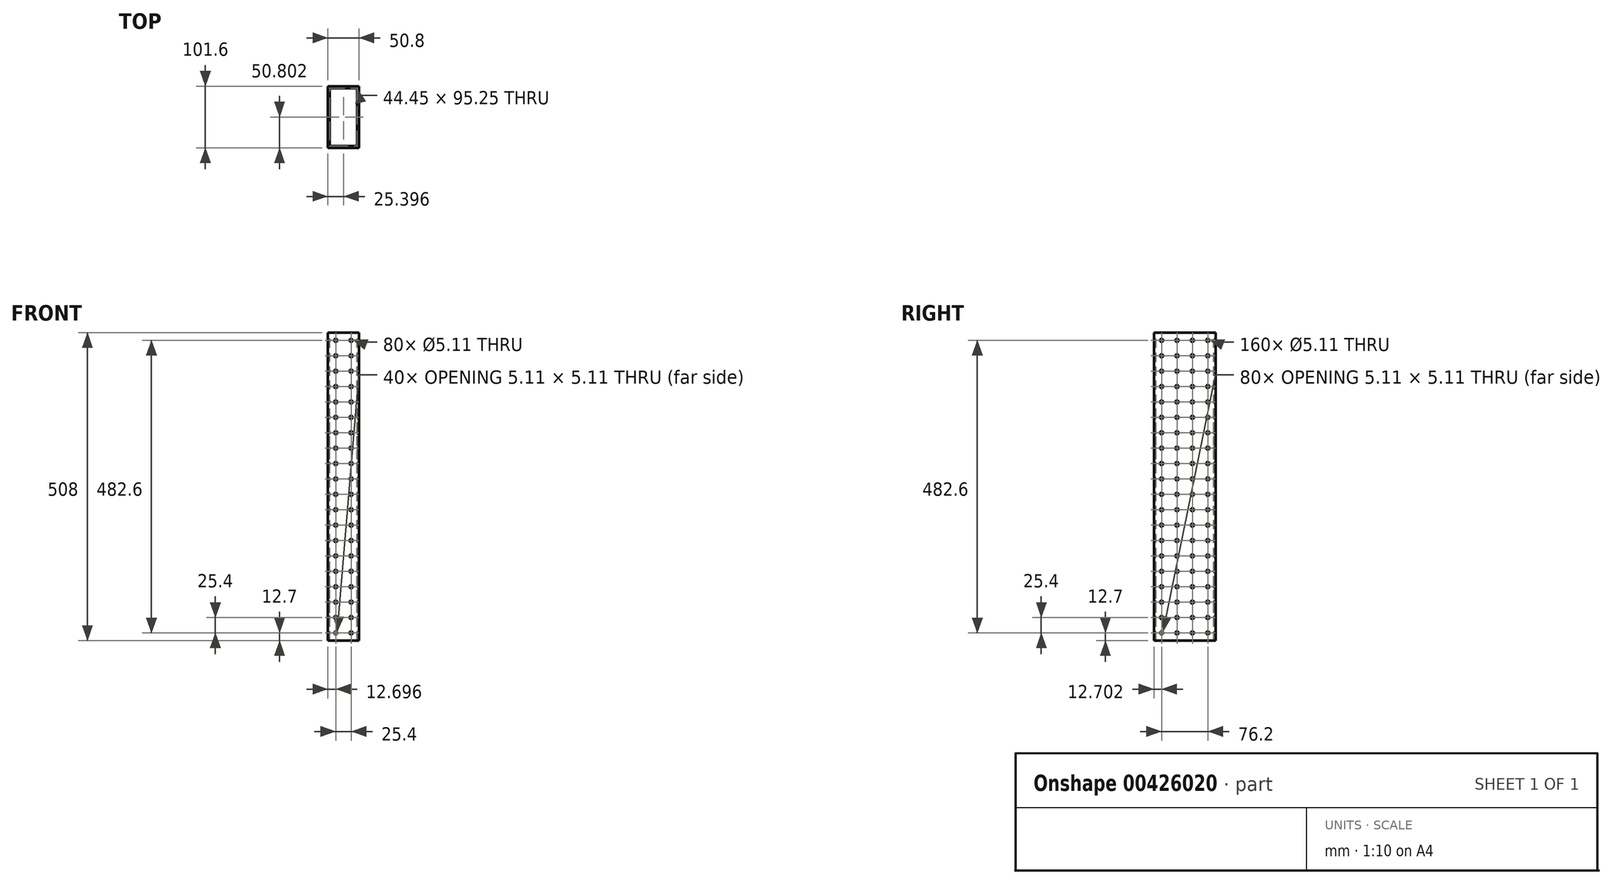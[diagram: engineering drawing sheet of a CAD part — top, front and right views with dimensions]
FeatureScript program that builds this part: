
annotation { "Feature Type Name" : "Feature", "Feature Type Description" : "" }
export const myFeature = defineFeature(function(context is Context, id is Id, definition is map)
    precondition{}
    {
        {
            var Q0;
            Q0=qCreatedBy(makeId("Top.planeOp"),FACE);
            var sketch = newSketch(context, id + "F0", { "sketchPlane" : qUnion([Q0])});
            skLineSegment(sketch, "E0.bottom", {"start": v(-16.8, 74.05) * mm, "end": v(34, 74.05) * mm});
            skLineSegment(sketch, "E0.top", {"start": v(-16.8, -27.55) * mm, "end": v(34, -27.55) * mm});
            skLineSegment(sketch, "E0.left", {"start": v(-16.8, 74.05) * mm, "end": v(-16.8, -27.55) * mm});
            skLineSegment(sketch, "E0.right", {"start": v(34, 74.05) * mm, "end": v(34, -27.55) * mm});
            skSolve(sketch);
        }
        {
            var Q0;
            Q0=makeQuery(id+"F0.imprint","IMPRINT",FACE,{"disambiguationData":[TD([[makeQuery(id+"F0.imprint","IMPRINT",EDGE,{"derivedFrom":sQuery(id+"F0.wireOp",EDGE,"E0.bottom")}),-1.0]])]});
            extrude(context, id + "F1", {"entities" : qUnion([Q0]), "depth" : 508 * mm});
        }
        {
            var Q0;
            Q0=makeQuery(id+"F1.opExtrude","CAP_FACE",FACE,{"disambiguationData":[OSD([sQuery(id+"F0.wireOp",EDGE,"E0.bottom"),sQuery(id+"F0.wireOp",EDGE,"E0.top"),sQuery(id+"F0.wireOp",EDGE,"E0.left"),sQuery(id+"F0.wireOp",EDGE,"E0.right")])],"isStart":false});
            var sketch = newSketch(context, id + "F2", { "sketchPlane" : qUnion([Q0])});
            skLineSegment(sketch, "E1.bottom", {"start": v(-13.63, 70.88) * mm, "end": v(30.82, 70.88) * mm});
            skLineSegment(sketch, "E1.top", {"start": v(-13.63, -24.37) * mm, "end": v(30.82, -24.37) * mm});
            skLineSegment(sketch, "E1.left", {"start": v(-13.63, 70.88) * mm, "end": v(-13.63, -24.37) * mm});
            skLineSegment(sketch, "E1.right", {"start": v(30.82, 70.88) * mm, "end": v(30.82, -24.37) * mm});
            skSolve(sketch);
        }
        {
            var Q0;
            Q0=makeQuery(id+"F2.imprint","IMPRINT",FACE,{"disambiguationData":[TD([[makeQuery(id+"F2.imprint","IMPRINT",EDGE,{"derivedFrom":sQuery(id+"F2.wireOp",EDGE,"E1.bottom")}),-1.0]])]});
            extrude(context, id + "F3", {"entities" : qUnion([Q0]), "operationType" : NewBodyOperationType.REMOVE, "oppositeDirection" : true, "depth" : 508 * mm});
        }
        {
            var Q0;
            Q0=makeQuery(id+"F1.opExtrude","SWEPT_FACE",FACE,{"disambiguationData":[OSD([sQuery(id+"F0.wireOp",EDGE,"E0.right")])]});
            var sketch = newSketch(context, id + "F4", { "sketchPlane" : qUnion([Q0])});
            skCircle(sketch, "E2", {"center": v(61.35, 495.3) * mm, "radius": 2.55 * mm});
            skCircle(sketch, "E3.0.1.0", {"center": v(61.35, 469.9) * mm, "radius": 2.55 * mm});
            skCircle(sketch, "E3.0.2.0", {"center": v(61.35, 444.5) * mm, "radius": 2.55 * mm});
            skCircle(sketch, "E3.0.3.0", {"center": v(61.35, 419.1) * mm, "radius": 2.55 * mm});
            skCircle(sketch, "E3.0.4.0", {"center": v(61.35, 393.7) * mm, "radius": 2.55 * mm});
            skCircle(sketch, "E3.0.5.0", {"center": v(61.35, 368.3) * mm, "radius": 2.55 * mm});
            skCircle(sketch, "E3.0.6.0", {"center": v(61.35, 342.9) * mm, "radius": 2.55 * mm});
            skCircle(sketch, "E3.0.7.0", {"center": v(61.35, 317.5) * mm, "radius": 2.55 * mm});
            skCircle(sketch, "E3.0.8.0", {"center": v(61.35, 292.1) * mm, "radius": 2.55 * mm});
            skCircle(sketch, "E3.0.9.0", {"center": v(61.35, 266.7) * mm, "radius": 2.55 * mm});
            skCircle(sketch, "E3.0.10.0", {"center": v(61.35, 241.3) * mm, "radius": 2.55 * mm});
            skCircle(sketch, "E3.0.11.0", {"center": v(61.35, 215.9) * mm, "radius": 2.55 * mm});
            skCircle(sketch, "E3.0.12.0", {"center": v(61.35, 190.5) * mm, "radius": 2.55 * mm});
            skCircle(sketch, "E3.0.13.0", {"center": v(61.35, 165.1) * mm, "radius": 2.55 * mm});
            skCircle(sketch, "E3.0.14.0", {"center": v(61.35, 139.7) * mm, "radius": 2.55 * mm});
            skCircle(sketch, "E3.0.15.0", {"center": v(61.35, 114.3) * mm, "radius": 2.55 * mm});
            skCircle(sketch, "E3.0.16.0", {"center": v(61.35, 88.9) * mm, "radius": 2.55 * mm});
            skCircle(sketch, "E3.0.17.0", {"center": v(61.35, 63.5) * mm, "radius": 2.55 * mm});
            skCircle(sketch, "E3.0.18.0", {"center": v(61.35, 38.1) * mm, "radius": 2.55 * mm});
            skCircle(sketch, "E3.0.19.0", {"center": v(61.35, 12.7) * mm, "radius": 2.55 * mm});
            skCircle(sketch, "E3.1.0.0", {"center": v(35.95, 495.3) * mm, "radius": 2.55 * mm});
            skCircle(sketch, "E3.1.1.0", {"center": v(35.95, 469.9) * mm, "radius": 2.55 * mm});
            skCircle(sketch, "E3.1.2.0", {"center": v(35.95, 444.5) * mm, "radius": 2.55 * mm});
            skCircle(sketch, "E3.1.3.0", {"center": v(35.95, 419.1) * mm, "radius": 2.55 * mm});
            skCircle(sketch, "E3.1.4.0", {"center": v(35.95, 393.7) * mm, "radius": 2.55 * mm});
            skCircle(sketch, "E3.1.5.0", {"center": v(35.95, 368.3) * mm, "radius": 2.55 * mm});
            skCircle(sketch, "E3.1.6.0", {"center": v(35.95, 342.9) * mm, "radius": 2.55 * mm});
            skCircle(sketch, "E3.1.7.0", {"center": v(35.95, 317.5) * mm, "radius": 2.55 * mm});
            skCircle(sketch, "E3.1.8.0", {"center": v(35.95, 292.1) * mm, "radius": 2.55 * mm});
            skCircle(sketch, "E3.1.9.0", {"center": v(35.95, 266.7) * mm, "radius": 2.55 * mm});
            skCircle(sketch, "E3.1.10.0", {"center": v(35.95, 241.3) * mm, "radius": 2.55 * mm});
            skCircle(sketch, "E3.1.11.0", {"center": v(35.95, 215.9) * mm, "radius": 2.55 * mm});
            skCircle(sketch, "E3.1.12.0", {"center": v(35.95, 190.5) * mm, "radius": 2.55 * mm});
            skCircle(sketch, "E3.1.13.0", {"center": v(35.95, 165.1) * mm, "radius": 2.55 * mm});
            skCircle(sketch, "E3.1.14.0", {"center": v(35.95, 139.7) * mm, "radius": 2.55 * mm});
            skCircle(sketch, "E3.1.15.0", {"center": v(35.95, 114.3) * mm, "radius": 2.55 * mm});
            skCircle(sketch, "E3.1.16.0", {"center": v(35.95, 88.9) * mm, "radius": 2.55 * mm});
            skCircle(sketch, "E3.1.17.0", {"center": v(35.95, 63.5) * mm, "radius": 2.55 * mm});
            skCircle(sketch, "E3.1.18.0", {"center": v(35.95, 38.1) * mm, "radius": 2.55 * mm});
            skCircle(sketch, "E3.1.19.0", {"center": v(35.95, 12.7) * mm, "radius": 2.55 * mm});
            skCircle(sketch, "E3.2.0.0", {"center": v(10.55, 495.3) * mm, "radius": 2.55 * mm});
            skCircle(sketch, "E3.2.1.0", {"center": v(10.55, 469.9) * mm, "radius": 2.55 * mm});
            skCircle(sketch, "E3.2.2.0", {"center": v(10.55, 444.5) * mm, "radius": 2.55 * mm});
            skCircle(sketch, "E3.2.3.0", {"center": v(10.55, 419.1) * mm, "radius": 2.55 * mm});
            skCircle(sketch, "E3.2.4.0", {"center": v(10.55, 393.7) * mm, "radius": 2.55 * mm});
            skCircle(sketch, "E3.2.5.0", {"center": v(10.55, 368.3) * mm, "radius": 2.55 * mm});
            skCircle(sketch, "E3.2.6.0", {"center": v(10.55, 342.9) * mm, "radius": 2.55 * mm});
            skCircle(sketch, "E3.2.7.0", {"center": v(10.55, 317.5) * mm, "radius": 2.55 * mm});
            skCircle(sketch, "E3.2.8.0", {"center": v(10.55, 292.1) * mm, "radius": 2.55 * mm});
            skCircle(sketch, "E3.2.9.0", {"center": v(10.55, 266.7) * mm, "radius": 2.55 * mm});
            skCircle(sketch, "E3.2.10.0", {"center": v(10.55, 241.3) * mm, "radius": 2.55 * mm});
            skCircle(sketch, "E3.2.11.0", {"center": v(10.55, 215.9) * mm, "radius": 2.55 * mm});
            skCircle(sketch, "E3.2.12.0", {"center": v(10.55, 190.5) * mm, "radius": 2.55 * mm});
            skCircle(sketch, "E3.2.13.0", {"center": v(10.55, 165.1) * mm, "radius": 2.55 * mm});
            skCircle(sketch, "E3.2.14.0", {"center": v(10.55, 139.7) * mm, "radius": 2.55 * mm});
            skCircle(sketch, "E3.2.15.0", {"center": v(10.55, 114.3) * mm, "radius": 2.55 * mm});
            skCircle(sketch, "E3.2.16.0", {"center": v(10.55, 88.9) * mm, "radius": 2.55 * mm});
            skCircle(sketch, "E3.2.17.0", {"center": v(10.55, 63.5) * mm, "radius": 2.55 * mm});
            skCircle(sketch, "E3.2.18.0", {"center": v(10.55, 38.1) * mm, "radius": 2.55 * mm});
            skCircle(sketch, "E3.2.19.0", {"center": v(10.55, 12.7) * mm, "radius": 2.55 * mm});
            skCircle(sketch, "E3.3.0.0", {"center": v(-14.85, 495.3) * mm, "radius": 2.55 * mm});
            skCircle(sketch, "E3.3.1.0", {"center": v(-14.85, 469.9) * mm, "radius": 2.55 * mm});
            skCircle(sketch, "E3.3.2.0", {"center": v(-14.85, 444.5) * mm, "radius": 2.55 * mm});
            skCircle(sketch, "E3.3.3.0", {"center": v(-14.85, 419.1) * mm, "radius": 2.55 * mm});
            skCircle(sketch, "E3.3.4.0", {"center": v(-14.85, 393.7) * mm, "radius": 2.55 * mm});
            skCircle(sketch, "E3.3.5.0", {"center": v(-14.85, 368.3) * mm, "radius": 2.55 * mm});
            skCircle(sketch, "E3.3.6.0", {"center": v(-14.85, 342.9) * mm, "radius": 2.55 * mm});
            skCircle(sketch, "E3.3.7.0", {"center": v(-14.85, 317.5) * mm, "radius": 2.55 * mm});
            skCircle(sketch, "E3.3.8.0", {"center": v(-14.85, 292.1) * mm, "radius": 2.55 * mm});
            skCircle(sketch, "E3.3.9.0", {"center": v(-14.85, 266.7) * mm, "radius": 2.55 * mm});
            skCircle(sketch, "E3.3.10.0", {"center": v(-14.85, 241.3) * mm, "radius": 2.55 * mm});
            skCircle(sketch, "E3.3.11.0", {"center": v(-14.85, 215.9) * mm, "radius": 2.55 * mm});
            skCircle(sketch, "E3.3.12.0", {"center": v(-14.85, 190.5) * mm, "radius": 2.55 * mm});
            skCircle(sketch, "E3.3.13.0", {"center": v(-14.85, 165.1) * mm, "radius": 2.55 * mm});
            skCircle(sketch, "E3.3.14.0", {"center": v(-14.85, 139.7) * mm, "radius": 2.55 * mm});
            skCircle(sketch, "E3.3.15.0", {"center": v(-14.85, 114.3) * mm, "radius": 2.55 * mm});
            skCircle(sketch, "E3.3.16.0", {"center": v(-14.85, 88.9) * mm, "radius": 2.55 * mm});
            skCircle(sketch, "E3.3.17.0", {"center": v(-14.85, 63.5) * mm, "radius": 2.55 * mm});
            skCircle(sketch, "E3.3.18.0", {"center": v(-14.85, 38.1) * mm, "radius": 2.55 * mm});
            skCircle(sketch, "E3.3.19.0", {"center": v(-14.85, 12.7) * mm, "radius": 2.55 * mm});
            skLineSegment(sketch, "E3.direction1", {"start": v(61.35, 495.3) * mm, "end": v(35.95, 495.3) * mm, "construction": true});
            skLineSegment(sketch, "E3.direction2", {"start": v(61.35, 495.3) * mm, "end": v(61.35, 469.9) * mm, "construction": true});
            skSolve(sketch);
        }
        {
            var Q0;
            Q0=sQuery(id+"F4.wireOp",VERTEX,"E3.1.15.0.center");
            var Q1;
            Q1=sQuery(id+"F4.wireOp",VERTEX,"E3.0.19.0.center");
            var Q2;
            Q2=sQuery(id+"F4.wireOp",VERTEX,"E3.3.7.0.center");
            var Q3;
            Q3=sQuery(id+"F4.wireOp",VERTEX,"E3.2.11.0.center");
            var Q4;
            Q4=sQuery(id+"F4.wireOp",VERTEX,"E3.3.0.0.center");
            var Q5;
            Q5=sQuery(id+"F4.wireOp",VERTEX,"E3.2.4.0.center");
            var Q6;
            Q6=sQuery(id+"F4.wireOp",VERTEX,"E3.1.8.0.center");
            var Q7;
            Q7=sQuery(id+"F4.wireOp",VERTEX,"E3.0.12.0.center");
            var Q8;
            Q8=sQuery(id+"F4.wireOp",VERTEX,"E3.3.16.0.center");
            var Q9;
            Q9=sQuery(id+"F4.wireOp",VERTEX,"E3.3.8.0.center");
            var Q10;
            Q10=sQuery(id+"F4.wireOp",VERTEX,"E3.2.12.0.center");
            var Q11;
            Q11=sQuery(id+"F4.wireOp",VERTEX,"E3.3.1.0.center");
            var Q12;
            Q12=sQuery(id+"F4.wireOp",VERTEX,"E3.2.5.0.center");
            var Q13;
            Q13=sQuery(id+"F4.wireOp",VERTEX,"E3.1.9.0.center");
            var Q14;
            Q14=sQuery(id+"F4.wireOp",VERTEX,"E3.0.13.0.center");
            var Q15;
            Q15=sQuery(id+"F4.wireOp",VERTEX,"E3.3.17.0.center");
            var Q16;
            Q16=sQuery(id+"F4.wireOp",VERTEX,"E3.1.16.0.center");
            var Q17;
            Q17=sQuery(id+"F4.wireOp",VERTEX,"E3.3.2.0.center");
            var Q18;
            Q18=sQuery(id+"F4.wireOp",VERTEX,"E3.2.6.0.center");
            var Q19;
            Q19=sQuery(id+"F4.wireOp",VERTEX,"E3.1.10.0.center");
            var Q20;
            Q20=sQuery(id+"F4.wireOp",VERTEX,"E3.0.14.0.center");
            var Q21;
            Q21=sQuery(id+"F4.wireOp",VERTEX,"E3.3.18.0.center");
            var Q22;
            Q22=sQuery(id+"F4.wireOp",VERTEX,"E3.1.17.0.center");
            var Q23;
            Q23=sQuery(id+"F4.wireOp",VERTEX,"E3.1.1.0.center");
            var Q24;
            Q24=sQuery(id+"F4.wireOp",VERTEX,"E3.3.9.0.center");
            var Q25;
            Q25=sQuery(id+"F4.wireOp",VERTEX,"E3.2.13.0.center");
            var Q26;
            Q26=sQuery(id+"F4.wireOp",VERTEX,"E3.3.3.0.center");
            var Q27;
            Q27=sQuery(id+"F4.wireOp",VERTEX,"E3.2.7.0.center");
            var Q28;
            Q28=sQuery(id+"F4.wireOp",VERTEX,"E3.1.11.0.center");
            var Q29;
            Q29=sQuery(id+"F4.wireOp",VERTEX,"E3.0.15.0.center");
            var Q30;
            Q30=sQuery(id+"F4.wireOp",VERTEX,"E3.3.19.0.center");
            var Q31;
            Q31=sQuery(id+"F4.wireOp",VERTEX,"E3.1.18.0.center");
            var Q32;
            Q32=sQuery(id+"F4.wireOp",VERTEX,"E3.1.2.0.center");
            var Q33;
            Q33=sQuery(id+"F4.wireOp",VERTEX,"E3.3.10.0.center");
            var Q34;
            Q34=sQuery(id+"F4.wireOp",VERTEX,"E3.2.14.0.center");
            var Q35;
            Q35=sQuery(id+"F4.wireOp",VERTEX,"E3.2.17.0.center");
            var Q36;
            Q36=sQuery(id+"F4.wireOp",VERTEX,"E3.3.4.0.center");
            var Q37;
            Q37=sQuery(id+"F4.wireOp",VERTEX,"E3.2.8.0.center");
            var Q38;
            Q38=sQuery(id+"F4.wireOp",VERTEX,"E3.2.1.0.center");
            var Q39;
            Q39=sQuery(id+"F4.wireOp",VERTEX,"E3.1.5.0.center");
            var Q40;
            Q40=sQuery(id+"F4.wireOp",VERTEX,"E3.1.12.0.center");
            var Q41;
            Q41=sQuery(id+"F4.wireOp",VERTEX,"E3.0.16.0.center");
            var Q42;
            Q42=sQuery(id+"F4.wireOp",VERTEX,"E3.3.13.0.center");
            var Q43;
            Q43=sQuery(id+"F4.wireOp",VERTEX,"E3.1.19.0.center");
            var Q44;
            Q44=sQuery(id+"F4.wireOp",VERTEX,"E3.1.3.0.center");
            var Q45;
            Q45=sQuery(id+"F4.wireOp",VERTEX,"E3.3.11.0.center");
            var Q46;
            Q46=sQuery(id+"F4.wireOp",VERTEX,"E3.2.15.0.center");
            var Q47;
            Q47=sQuery(id+"F4.wireOp",VERTEX,"E3.2.18.0.center");
            var Q48;
            Q48=sQuery(id+"F4.wireOp",VERTEX,"E3.3.5.0.center");
            var Q49;
            Q49=sQuery(id+"F4.wireOp",VERTEX,"E3.2.2.0.center");
            var Q50;
            Q50=sQuery(id+"F4.wireOp",VERTEX,"E3.2.9.0.center");
            var Q51;
            Q51=sQuery(id+"F4.wireOp",VERTEX,"E3.1.6.0.center");
            var Q52;
            Q52=sQuery(id+"F4.wireOp",VERTEX,"E3.1.13.0.center");
            var Q53;
            Q53=sQuery(id+"F4.wireOp",VERTEX,"E3.0.17.0.center");
            var Q54;
            Q54=sQuery(id+"F4.wireOp",VERTEX,"E3.3.14.0.center");
            var Q55;
            Q55=sQuery(id+"F4.wireOp",VERTEX,"E3.2.0.0.center");
            var Q56;
            Q56=sQuery(id+"F4.wireOp",VERTEX,"E3.1.4.0.center");
            var Q57;
            Q57=sQuery(id+"F4.wireOp",VERTEX,"E3.0.9.0.center");
            var Q58;
            Q58=sQuery(id+"F4.wireOp",VERTEX,"E3.0.10.0.center");
            var Q59;
            Q59=sQuery(id+"F4.wireOp",VERTEX,"E3.3.12.0.center");
            var Q60;
            Q60=sQuery(id+"F4.wireOp",VERTEX,"E3.2.16.0.center");
            var Q61;
            Q61=sQuery(id+"F4.wireOp",VERTEX,"E3.0.11.0.center");
            var Q62;
            Q62=sQuery(id+"F4.wireOp",VERTEX,"E3.direction1.end");
            var Q63;
            Q63=sQuery(id+"F4.wireOp",VERTEX,"E2.center");
            var Q64;
            Q64=sQuery(id+"F4.wireOp",VERTEX,"E3.3.6.0.center");
            var Q65;
            Q65=sQuery(id+"F4.wireOp",VERTEX,"E3.2.19.0.center");
            var Q66;
            Q66=sQuery(id+"F4.wireOp",VERTEX,"E3.2.10.0.center");
            var Q67;
            Q67=sQuery(id+"F4.wireOp",VERTEX,"E3.2.3.0.center");
            var Q68;
            Q68=sQuery(id+"F4.wireOp",VERTEX,"E3.1.7.0.center");
            var Q69;
            Q69=sQuery(id+"F4.wireOp",VERTEX,"E3.1.14.0.center");
            var Q70;
            Q70=sQuery(id+"F4.wireOp",VERTEX,"E3.0.18.0.center");
            var Q71;
            Q71=sQuery(id+"F4.wireOp",VERTEX,"E3.0.1.0.center");
            var Q72;
            Q72=sQuery(id+"F4.wireOp",VERTEX,"E3.3.15.0.center");
            var Q73;
            Q73=sQuery(id+"F4.wireOp",VERTEX,"E3.0.2.0.center");
            var Q74;
            Q74=sQuery(id+"F4.wireOp",VERTEX,"E3.0.3.0.center");
            var Q75;
            Q75=sQuery(id+"F4.wireOp",VERTEX,"E3.0.4.0.center");
            var Q76;
            Q76=sQuery(id+"F4.wireOp",VERTEX,"E3.0.5.0.center");
            var Q77;
            Q77=sQuery(id+"F4.wireOp",VERTEX,"E3.0.6.0.center");
            var Q78;
            Q78=sQuery(id+"F4.wireOp",VERTEX,"E3.0.7.0.center");
            var Q79;
            Q79=sQuery(id+"F4.wireOp",VERTEX,"E3.0.8.0.center");
            var Q80;
            Q80=makeQuery(id+"F1.opExtrude","SWEPT_BODY",BODY,{"disambiguationData":[OSD([sQuery(id+"F0.wireOp",EDGE,"E0.bottom"),sQuery(id+"F0.wireOp",EDGE,"E0.top"),sQuery(id+"F0.wireOp",EDGE,"E0.left"),sQuery(id+"F0.wireOp",EDGE,"E0.right")])]});
            hole(context, id + "F5", {"style" : HoleStyle.SIMPLE, "endStyle" : HoleEndStyle.THROUGH, "holeDiameter" : 5.1 * mm, "isTappedThrough" : true, "tappedDepth" : 12.7 * mm, "tapClearance" : 3, "locations" : qUnion([Q0, Q1, Q2, Q3, Q4, Q5, Q6, Q7, Q8, Q9, Q10, Q11, Q12, Q13, Q14, Q15, Q16, Q17, Q18, Q19, Q20, Q21, Q22, Q23, Q24, Q25, Q26, Q27, Q28, Q29, Q30, Q31, Q32, Q33, Q34, Q35, Q36, Q37, Q38, Q39, Q40, Q41, Q42, Q43, Q44, Q45, Q46, Q47, Q48, Q49, Q50, Q51, Q52, Q53, Q54, Q55, Q56, Q57, Q58, Q59, Q60, Q61, Q62, Q63, Q64, Q65, Q66, Q67, Q68, Q69, Q70, Q71, Q72, Q73, Q74, Q75, Q76, Q77, Q78, Q79]), "scope" : qUnion([Q80])});
        }
        {
            var Q0;
            Q0=makeQuery(id+"F1.opExtrude","SWEPT_FACE",FACE,{"disambiguationData":[OSD([sQuery(id+"F0.wireOp",EDGE,"E0.bottom")])]});
            var sketch = newSketch(context, id + "F6", { "sketchPlane" : qUnion([Q0])});
            skCircle(sketch, "E4", {"center": v(-21.3, 495.3) * mm, "radius": 2.55 * mm});
            skCircle(sketch, "E5.0.1.0", {"center": v(-21.3, 469.9) * mm, "radius": 2.55 * mm});
            skCircle(sketch, "E5.0.2.0", {"center": v(-21.3, 444.5) * mm, "radius": 2.55 * mm});
            skCircle(sketch, "E5.0.3.0", {"center": v(-21.3, 419.1) * mm, "radius": 2.55 * mm});
            skCircle(sketch, "E5.0.4.0", {"center": v(-21.3, 393.7) * mm, "radius": 2.55 * mm});
            skCircle(sketch, "E5.0.5.0", {"center": v(-21.3, 368.3) * mm, "radius": 2.55 * mm});
            skCircle(sketch, "E5.0.6.0", {"center": v(-21.3, 342.9) * mm, "radius": 2.55 * mm});
            skCircle(sketch, "E5.0.7.0", {"center": v(-21.3, 317.5) * mm, "radius": 2.55 * mm});
            skCircle(sketch, "E5.0.8.0", {"center": v(-21.3, 292.1) * mm, "radius": 2.55 * mm});
            skCircle(sketch, "E5.0.9.0", {"center": v(-21.3, 266.7) * mm, "radius": 2.55 * mm});
            skCircle(sketch, "E5.0.10.0", {"center": v(-21.3, 241.3) * mm, "radius": 2.55 * mm});
            skCircle(sketch, "E5.0.11.0", {"center": v(-21.3, 215.9) * mm, "radius": 2.55 * mm});
            skCircle(sketch, "E5.0.12.0", {"center": v(-21.3, 190.5) * mm, "radius": 2.55 * mm});
            skCircle(sketch, "E5.0.13.0", {"center": v(-21.3, 165.1) * mm, "radius": 2.55 * mm});
            skCircle(sketch, "E5.0.14.0", {"center": v(-21.3, 139.7) * mm, "radius": 2.55 * mm});
            skCircle(sketch, "E5.0.15.0", {"center": v(-21.3, 114.3) * mm, "radius": 2.55 * mm});
            skCircle(sketch, "E5.0.16.0", {"center": v(-21.3, 88.9) * mm, "radius": 2.55 * mm});
            skCircle(sketch, "E5.0.17.0", {"center": v(-21.3, 63.5) * mm, "radius": 2.55 * mm});
            skCircle(sketch, "E5.0.18.0", {"center": v(-21.3, 38.1) * mm, "radius": 2.55 * mm});
            skCircle(sketch, "E5.0.19.0", {"center": v(-21.3, 12.7) * mm, "radius": 2.55 * mm});
            skCircle(sketch, "E5.1.0.0", {"center": v(4.1, 495.3) * mm, "radius": 2.55 * mm});
            skCircle(sketch, "E5.1.1.0", {"center": v(4.1, 469.9) * mm, "radius": 2.55 * mm});
            skCircle(sketch, "E5.1.2.0", {"center": v(4.1, 444.5) * mm, "radius": 2.55 * mm});
            skCircle(sketch, "E5.1.3.0", {"center": v(4.1, 419.1) * mm, "radius": 2.55 * mm});
            skCircle(sketch, "E5.1.4.0", {"center": v(4.1, 393.7) * mm, "radius": 2.55 * mm});
            skCircle(sketch, "E5.1.5.0", {"center": v(4.1, 368.3) * mm, "radius": 2.55 * mm});
            skCircle(sketch, "E5.1.6.0", {"center": v(4.1, 342.9) * mm, "radius": 2.55 * mm});
            skCircle(sketch, "E5.1.7.0", {"center": v(4.1, 317.5) * mm, "radius": 2.55 * mm});
            skCircle(sketch, "E5.1.8.0", {"center": v(4.1, 292.1) * mm, "radius": 2.55 * mm});
            skCircle(sketch, "E5.1.9.0", {"center": v(4.1, 266.7) * mm, "radius": 2.55 * mm});
            skCircle(sketch, "E5.1.10.0", {"center": v(4.1, 241.3) * mm, "radius": 2.55 * mm});
            skCircle(sketch, "E5.1.11.0", {"center": v(4.1, 215.9) * mm, "radius": 2.55 * mm});
            skCircle(sketch, "E5.1.12.0", {"center": v(4.1, 190.5) * mm, "radius": 2.55 * mm});
            skCircle(sketch, "E5.1.13.0", {"center": v(4.1, 165.1) * mm, "radius": 2.55 * mm});
            skCircle(sketch, "E5.1.14.0", {"center": v(4.1, 139.7) * mm, "radius": 2.55 * mm});
            skCircle(sketch, "E5.1.15.0", {"center": v(4.1, 114.3) * mm, "radius": 2.55 * mm});
            skCircle(sketch, "E5.1.16.0", {"center": v(4.1, 88.9) * mm, "radius": 2.55 * mm});
            skCircle(sketch, "E5.1.17.0", {"center": v(4.1, 63.5) * mm, "radius": 2.55 * mm});
            skCircle(sketch, "E5.1.18.0", {"center": v(4.1, 38.1) * mm, "radius": 2.55 * mm});
            skCircle(sketch, "E5.1.19.0", {"center": v(4.1, 12.7) * mm, "radius": 2.55 * mm});
            skLineSegment(sketch, "E5.direction1", {"start": v(-21.3, 495.3) * mm, "end": v(4.1, 495.3) * mm, "construction": true});
            skLineSegment(sketch, "E5.direction2", {"start": v(-21.3, 495.3) * mm, "end": v(-21.3, 469.9) * mm, "construction": true});
            skSolve(sketch);
        }
        {
            var Q0;
            Q0=sQuery(id+"F6.wireOp",VERTEX,"E5.0.11.0.center");
            var Q1;
            Q1=sQuery(id+"F6.wireOp",VERTEX,"E5.0.10.0.center");
            var Q2;
            Q2=sQuery(id+"F6.wireOp",VERTEX,"E5.0.15.0.center");
            var Q3;
            Q3=sQuery(id+"F6.wireOp",VERTEX,"E5.1.11.0.center");
            var Q4;
            Q4=sQuery(id+"F6.wireOp",VERTEX,"E5.1.2.0.center");
            var Q5;
            Q5=sQuery(id+"F6.wireOp",VERTEX,"E5.1.18.0.center");
            var Q6;
            Q6=sQuery(id+"F6.wireOp",VERTEX,"E5.0.9.0.center");
            var Q7;
            Q7=sQuery(id+"F6.wireOp",VERTEX,"E5.0.8.0.center");
            var Q8;
            Q8=sQuery(id+"F6.wireOp",VERTEX,"E5.0.7.0.center");
            var Q9;
            Q9=sQuery(id+"F6.wireOp",VERTEX,"E5.0.2.0.center");
            var Q10;
            Q10=sQuery(id+"F6.wireOp",VERTEX,"E5.0.1.0.center");
            var Q11;
            Q11=sQuery(id+"F6.wireOp",VERTEX,"E5.0.4.0.center");
            var Q12;
            Q12=sQuery(id+"F6.wireOp",VERTEX,"E5.0.3.0.center");
            var Q13;
            Q13=sQuery(id+"F6.wireOp",VERTEX,"E5.0.6.0.center");
            var Q14;
            Q14=sQuery(id+"F6.wireOp",VERTEX,"E5.0.5.0.center");
            var Q15;
            Q15=sQuery(id+"F6.wireOp",VERTEX,"E5.0.14.0.center");
            var Q16;
            Q16=sQuery(id+"F6.wireOp",VERTEX,"E5.1.10.0.center");
            var Q17;
            Q17=sQuery(id+"F6.wireOp",VERTEX,"E5.1.1.0.center");
            var Q18;
            Q18=sQuery(id+"F6.wireOp",VERTEX,"E5.1.17.0.center");
            var Q19;
            Q19=sQuery(id+"F6.wireOp",VERTEX,"E5.direction1.start");
            var Q20;
            Q20=sQuery(id+"F6.wireOp",VERTEX,"E5.0.18.0.center");
            var Q21;
            Q21=sQuery(id+"F6.wireOp",VERTEX,"E5.1.7.0.center");
            var Q22;
            Q22=sQuery(id+"F6.wireOp",VERTEX,"E5.1.14.0.center");
            var Q23;
            Q23=sQuery(id+"F6.wireOp",VERTEX,"E5.0.17.0.center");
            var Q24;
            Q24=sQuery(id+"F6.wireOp",VERTEX,"E5.1.6.0.center");
            var Q25;
            Q25=sQuery(id+"F6.wireOp",VERTEX,"E5.1.13.0.center");
            var Q26;
            Q26=sQuery(id+"F6.wireOp",VERTEX,"E5.0.13.0.center");
            var Q27;
            Q27=sQuery(id+"F6.wireOp",VERTEX,"E5.1.9.0.center");
            var Q28;
            Q28=sQuery(id+"F6.wireOp",VERTEX,"E5.1.4.0.center");
            var Q29;
            Q29=sQuery(id+"F6.wireOp",VERTEX,"E5.1.0.0.center");
            var Q30;
            Q30=sQuery(id+"F6.wireOp",VERTEX,"E5.1.16.0.center");
            var Q31;
            Q31=sQuery(id+"F6.wireOp",VERTEX,"E5.0.16.0.center");
            var Q32;
            Q32=sQuery(id+"F6.wireOp",VERTEX,"E5.1.5.0.center");
            var Q33;
            Q33=sQuery(id+"F6.wireOp",VERTEX,"E5.1.12.0.center");
            var Q34;
            Q34=sQuery(id+"F6.wireOp",VERTEX,"E5.0.12.0.center");
            var Q35;
            Q35=sQuery(id+"F6.wireOp",VERTEX,"E5.1.8.0.center");
            var Q36;
            Q36=sQuery(id+"F6.wireOp",VERTEX,"E5.1.3.0.center");
            var Q37;
            Q37=sQuery(id+"F6.wireOp",VERTEX,"E5.1.19.0.center");
            var Q38;
            Q38=sQuery(id+"F6.wireOp",VERTEX,"E5.0.19.0.center");
            var Q39;
            Q39=sQuery(id+"F6.wireOp",VERTEX,"E5.1.15.0.center");
            var Q40;
            Q40=makeQuery(id+"F1.opExtrude","SWEPT_BODY",BODY,{"disambiguationData":[OSD([sQuery(id+"F0.wireOp",EDGE,"E0.bottom"),sQuery(id+"F0.wireOp",EDGE,"E0.top"),sQuery(id+"F0.wireOp",EDGE,"E0.left"),sQuery(id+"F0.wireOp",EDGE,"E0.right")])]});
            hole(context, id + "F7", {"style" : HoleStyle.SIMPLE, "endStyle" : HoleEndStyle.THROUGH, "holeDiameter" : 5.1 * mm, "isTappedThrough" : true, "tappedDepth" : 12.7 * mm, "tapClearance" : 3, "locations" : qUnion([Q0, Q1, Q2, Q3, Q4, Q5, Q6, Q7, Q8, Q9, Q10, Q11, Q12, Q13, Q14, Q15, Q16, Q17, Q18, Q19, Q20, Q21, Q22, Q23, Q24, Q25, Q26, Q27, Q28, Q29, Q30, Q31, Q32, Q33, Q34, Q35, Q36, Q37, Q38, Q39]), "scope" : qUnion([Q40])});
        }
    });
